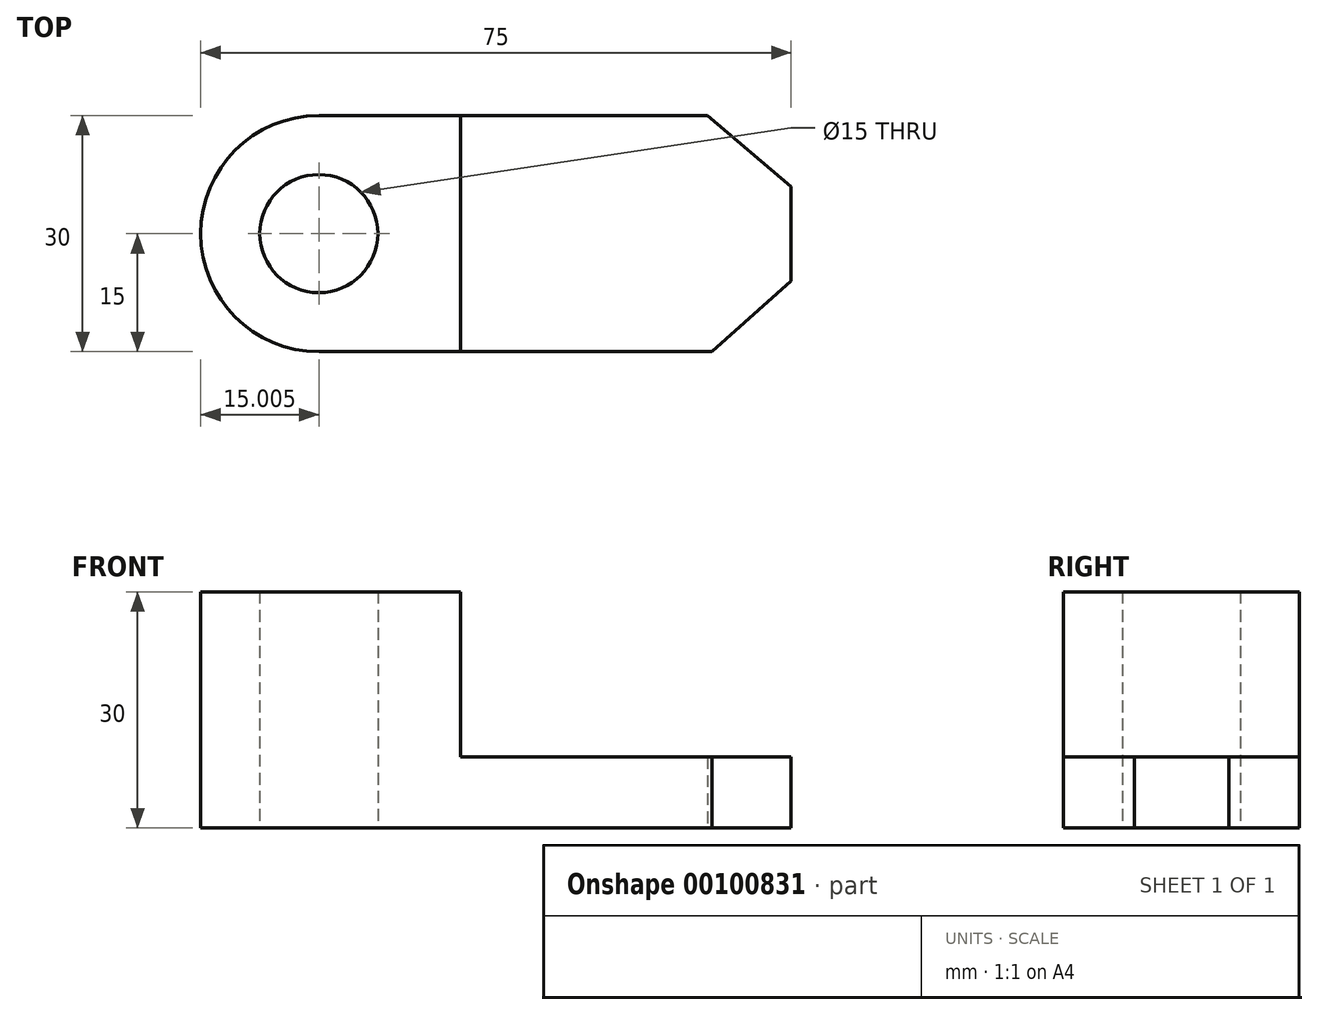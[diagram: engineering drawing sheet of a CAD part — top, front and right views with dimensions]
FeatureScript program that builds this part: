
annotation { "Feature Type Name" : "Feature", "Feature Type Description" : "" }
export const myFeature = defineFeature(function(context is Context, id is Id, definition is map)
    precondition{}
    {
        {
            var Q0;
            Q0=qCreatedBy(makeId("Top.planeOp"),FACE);
            var sketch = newSketch(context, id + "F0", { "sketchPlane" : qUnion([Q0])});
            skLineSegment(sketch, "E0.bottom", {"start": v(17.88, 0) * mm, "end": v(-0.12, 0) * mm});
            skLineSegment(sketch, "E0.top", {"start": v(17.88, 30) * mm, "end": v(-0.12, 30) * mm});
            skLineSegment(sketch, "E0.left", {"start": v(17.88, 0) * mm, "end": v(17.88, 30) * mm});
            skArc(sketch, "E1", {"start": v(-0.12, 30) * mm, "mid": v(-15.12, 15) * mm, "end": v(-0.12, 0) * mm});
            skCircle(sketch, "E2", {"center": v(-0.12, 15) * mm, "radius": 7.5 * mm});
            skLineSegment(sketch, "E3", {"start": v(49.23, 30) * mm, "end": v(59.88, 21) * mm});
            skLineSegment(sketch, "E4", {"start": v(59.88, 21) * mm, "end": v(59.88, 9) * mm});
            skLineSegment(sketch, "E5", {"start": v(59.88, 9) * mm, "end": v(49.8, 0) * mm});
            skLineSegment(sketch, "E6", {"start": v(49.23, 30) * mm, "end": v(17.88, 30) * mm});
            skLineSegment(sketch, "E7", {"start": v(49.8, 0) * mm, "end": v(17.88, 0) * mm});
            skSolve(sketch);
        }
        {
            var Q0;
            Q0 = qSketchRegion(id + "F0", true);
            extrude(context, id + "F1", {"entities" : qUnion([Q0]), "depth" : 9 * mm});
        }
        {
            var Q0;
            Q0=makeQuery(id+"F1.opExtrude","CAP_FACE",FACE,{"disambiguationData":[OSD([sQuery(id+"F0.wireOp",EDGE,"E0.bottom"),sQuery(id+"F0.wireOp",EDGE,"E0.top"),sQuery(id+"F0.wireOp",EDGE,"E1"),sQuery(id+"F0.wireOp",EDGE,"E2"),sQuery(id+"F0.wireOp",EDGE,"E3"),sQuery(id+"F0.wireOp",EDGE,"E4"),sQuery(id+"F0.wireOp",EDGE,"E5"),sQuery(id+"F0.wireOp",EDGE,"E6"),sQuery(id+"F0.wireOp",EDGE,"E7")])],"isStart":false});
            var sketch = newSketch(context, id + "F2", { "sketchPlane" : qUnion([Q0])});
            skLineSegment(sketch, "E8.right", {"start": v(17.88, 30) * mm, "end": v(17.88, 0) * mm});
            skSolve(sketch);
        }
        {
            var Q0;
            {var subQ2=sQuery(id+"F2.wireOp",EDGE,"E8.right");Q0=makeQuery(id+"F2.imprint","IMPRINT",FACE,{"disambiguationData":[TD([[makeQuery(id+"F2.imprint","IMPRINT",EDGE,{"derivedFrom":subQ2}),-1.0]])]});}
            extrude(context, id + "F3", {"entities" : qUnion([Q0]), "operationType" : NewBodyOperationType.ADD, "depth" : 21 * mm});
        }
    });
